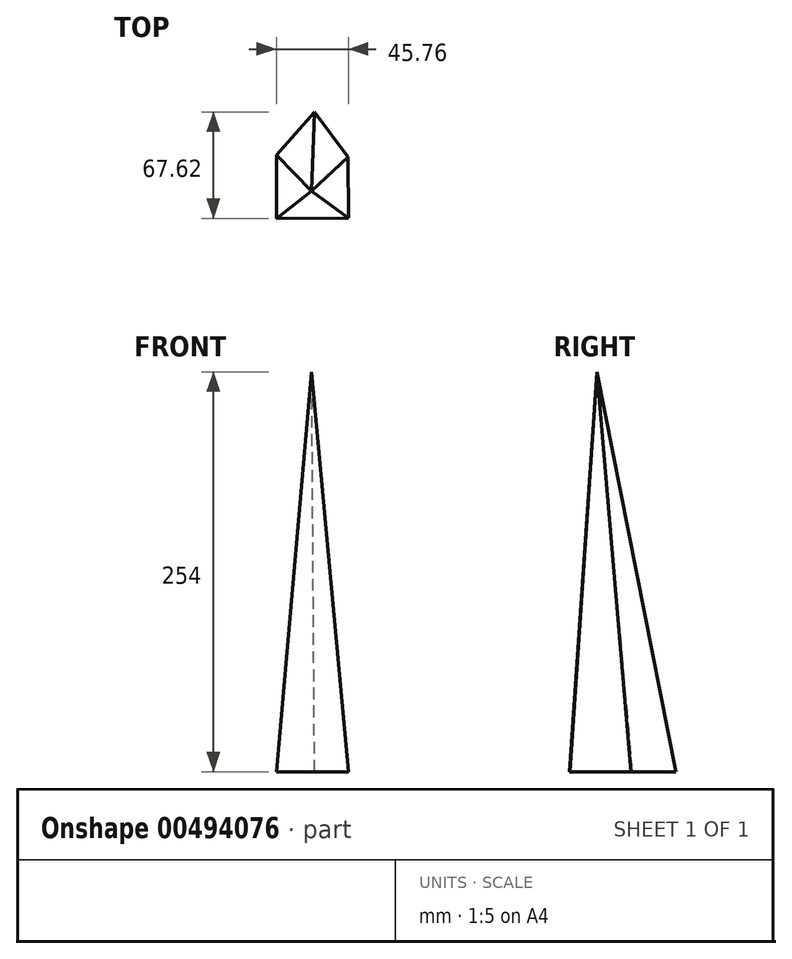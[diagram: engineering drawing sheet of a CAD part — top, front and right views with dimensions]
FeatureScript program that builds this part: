
annotation { "Feature Type Name" : "Feature", "Feature Type Description" : "" }
export const myFeature = defineFeature(function(context is Context, id is Id, definition is map)
    precondition{}
    {
        {
            var Q0;
            Q0=qCreatedBy(makeId("Top.planeOp"),FACE);
            var sketch = newSketch(context, id + "F0", { "sketchPlane" : qUnion([Q0])});
            skLineSegment(sketch, "E0", {"start": v(0, 19.1) * mm, "end": v(-24.2, -8.3) * mm});
            skLineSegment(sketch, "E1", {"start": v(-24.2, -8.3) * mm, "end": v(-24.2, -48.53) * mm});
            skLineSegment(sketch, "E2", {"start": v(-24.2, -48.53) * mm, "end": v(21.57, -48.24) * mm});
            skLineSegment(sketch, "E3", {"start": v(21.57, -48.24) * mm, "end": v(21.32, -9.47) * mm});
            skLineSegment(sketch, "E4", {"start": v(21.32, -9.47) * mm, "end": v(0, 19.1) * mm});
            skSolve(sketch);
        }
        {
            var Q0;
            Q0=qCreatedBy(makeId("Top.planeOp"),FACE);
            cPlane(context, id + "F1", {"entities" : qUnion([Q0]), "cplaneType" : CPlaneType.OFFSET, "offset" : 254 * mm, "width" : 152.4 * mm, "height" : 152.4 * mm});
        }
        {
            var Q0;
            Q0=qCreatedBy(id+"F1.planeOp",FACE);
            var sketch = newSketch(context, id + "F2", { "sketchPlane" : qUnion([Q0])});
            skPoint(sketch, "E5", {"position": v(-1.74, -31.11) * mm});
            skSolve(sketch);
        }
        {
            var Q0;
            Q0=makeQuery(id+"F0.imprint","IMPRINT",FACE,{"disambiguationData":[TD([[makeQuery(id+"F0.imprint","IMPRINT",EDGE,{"derivedFrom":sQuery(id+"F0.wireOp",EDGE,"E0")}),1.0]])]});
            var Q1;
            Q1=sQuery(id+"F2.wireOp",VERTEX,"E5");
            loft(context, id + "F3", {"sheetProfilesArray" : [{ "sheetProfileEntities" : qUnion([Q0]) }, { "sheetProfileEntities" : qUnion([Q1]) }]});
        }
    });
